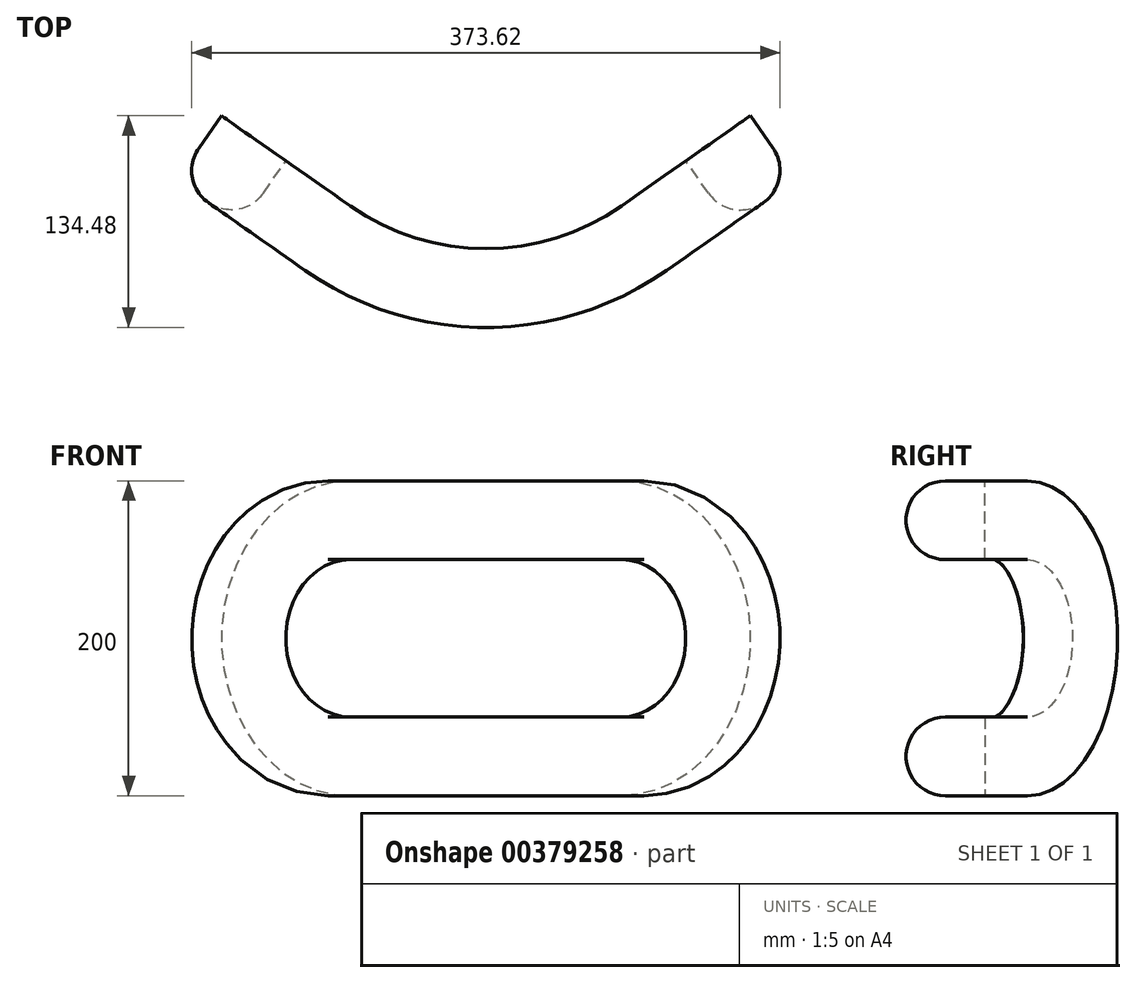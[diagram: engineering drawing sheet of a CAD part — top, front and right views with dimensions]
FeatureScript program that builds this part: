
annotation { "Feature Type Name" : "Feature", "Feature Type Description" : "" }
export const myFeature = defineFeature(function(context is Context, id is Id, definition is map)
    precondition{}
    {
        {
            var Q0;
            Q0=qCreatedBy(makeId("Top.planeOp"),FACE);
            var sketch = newSketch(context, id + "F0", { "sketchPlane" : qUnion([Q0])});
            skArc(sketch, "E0", {"start": v(86.04, -43.77) * mm, "mid": v(45.1, -63.95) * mm, "end": v(0, -70.9) * mm});
            skLineSegment(sketch, "E1", {"start": v(0, 79.1) * mm, "end": v(86.04, -43.77) * mm, "construction": true});
            skLineSegment(sketch, "E2", {"start": v(86.04, -43.77) * mm, "end": v(167.95, 13.6) * mm});
            skLineSegment(sketch, "E3", {"start": v(-7.3, -69.9) * mm, "end": v(-7.3, -69.9) * mm});
            skLineSegment(sketch, "E4", {"start": v(-17.04, -69.11) * mm, "end": v(-17.04, -69.11) * mm});
            skSolve(sketch);
        }
        {
            var Q0;
            Q0=sQuery(id+"F0.wireOp",EDGE,"E2");
            var Q1;
            Q1=sQuery(id+"F0.wireOp",EDGE,"E0");
            extrude(context, id + "F1", {"bodyType" : ToolBodyType.SURFACE, "surfaceEntities" : qUnion([Q0, Q1]), "depth" : 100 * mm});
        }
        {
            var Q0;
            Q0=makeQuery(id+"F1.opExtrude","SWEPT_FACE",FACE,{"disambiguationData":[OSD([sQuery(id+"F0.wireOp",EDGE,"E2")])]});
            var sketch = newSketch(context, id + "F2", { "sketchPlane" : qUnion([Q0])});
            skArc(sketch, "E5", {"start": v(145.37, 0) * mm, "mid": v(116.08, 70.71) * mm, "end": v(45.37, 100) * mm});
            skSolve(sketch);
        }
        {
            var Q0;
            Q0=qCreatedBy(makeId("Right.planeOp"),FACE);
            var sketch = newSketch(context, id + "F3", { "sketchPlane" : qUnion([Q0])});
            skLineSegment(sketch, "E6.bottom", {"start": v(-70.9, 100) * mm, "end": v(-95.9, 100) * mm});
            skLineSegment(sketch, "E6.top", {"start": v(-70.9, 50) * mm, "end": v(-95.9, 50) * mm});
            skLineSegment(sketch, "E6.left", {"start": v(-70.9, 100) * mm, "end": v(-70.9, 50) * mm});
            skLineSegment(sketch, "E6.right", {"start": v(-95.9, 100) * mm, "end": v(-95.9, 50) * mm, "construction": true});
            skArc(sketch, "E7", {"start": v(-95.9, 100) * mm, "mid": v(-120.9, 75) * mm, "end": v(-95.9, 50) * mm});
            skSolve(sketch);
        }
        {
            var Q0;
            Q0=makeQuery(id+"F3.imprint","IMPRINT",FACE,{"disambiguationData":[TD([[makeQuery(id+"F3.imprint","IMPRINT",EDGE,{"derivedFrom":sQuery(id+"F3.wireOp",EDGE,"E6.bottom")}),1.0]])]});
            var Q1;
            Q1=makeQuery(id+"F1.opExtrude","CAP_EDGE",EDGE,{"disambiguationData":[OSD([sQuery(id+"F0.wireOp",EDGE,"E0")])],"isStart":false});
            var Q2;
            Q2=sQuery(id+"F2.wireOp",EDGE,"E5");
            sweep(context, id + "F4", {"profiles" : qUnion([Q0]), "path" : qUnion([Q1, Q2])});
        }
        {
            var Q0;
            Q0=makeQuery(id+"F4.opSweep","SWEPT_BODY",BODY,{"disambiguationData":[OSD([sQuery(id+"F2.wireOp",EDGE,"E5"),sQuery(id+"F3.wireOp",EDGE,"E6.bottom"),sQuery(id+"F3.wireOp",EDGE,"E6.top"),sQuery(id+"F3.wireOp",EDGE,"E6.left"),sQuery(id+"F3.wireOp",EDGE,"E7")])]});
            var Q1;
            Q1=qCreatedBy(makeId("Top.planeOp"),FACE);
            mirror(context, id + "F5", {"operationType" : NewBodyOperationType.ADD, "entities" : qUnion([Q0]), "mirrorPlane" : qUnion([Q1])});
        }
        {
            var Q0;
            Q0=makeQuery(id+"F4.opSweep","SWEPT_BODY",BODY,{"disambiguationData":[OSD([sQuery(id+"F2.wireOp",EDGE,"E5"),sQuery(id+"F3.wireOp",EDGE,"E6.bottom"),sQuery(id+"F3.wireOp",EDGE,"E6.top"),sQuery(id+"F3.wireOp",EDGE,"E6.left"),sQuery(id+"F3.wireOp",EDGE,"E7")])]});
            var Q1;
            Q1=qCreatedBy(makeId("Right.planeOp"),FACE);
            mirror(context, id + "F6", {"operationType" : NewBodyOperationType.ADD, "entities" : qUnion([Q0]), "mirrorPlane" : qUnion([Q1])});
        }
    });
